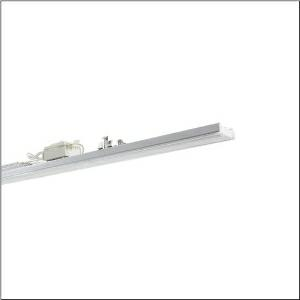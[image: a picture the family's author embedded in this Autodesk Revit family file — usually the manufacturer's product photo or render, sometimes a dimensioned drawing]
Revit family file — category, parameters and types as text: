
# Revit family: licross_21_recessed_ho_52tl12mn4fxm
name_source: partatom
category: Lighting Fixtures
units: mm (PartAtom-declared; Revit-internal decimal feet)

## family parameters
Cut with Voids When Loaded = No
Host = Face
Light Source = No
Part Type = Normal
Room Calculation Point = No
Round Connector Dimension = Use Diameter
Shared = No

## types (1)
- --- (1 x LED, 15100 lm, 83.1 W, 4000K)
    Apparent Load = 83 VA
    CIE Flux Codes = 69 91 98 100 100
    Color Rendering = 80
    Color Temperature = 4000K
    Default Elevation = 1800 mm
    Description = Licross 21 Recessed HO, luminaire insert, of sheet steel, galvanised, coil coated, white, length: 1.500mm, width: 66mm, height: 67mm, LED rated luminous flux: 15.100lm, light colour: 840, SDCM (Standard Deviation of Colour Matching)MacAdam ≤ 3 SDCM (initial), control gear: ON/OFF Multilumen, with plug, 3-pole, with phase selection, mains connection: 220..240V, AC, 50/60Hz, rated input power: 83W, internal wiring halogen-free, primary optical cover: cover, of PMMA, light emission: direct distribution, primary light characteristic: symmetric, protection rating (complete): IP40, insulation class (complete): insulation class I (protective earthing), certification: CE, ENEC, VDE, UKCA, protection symbol: D if used in an environment without relevant dust loads with corresponding accessories, impact resistance: IK06, permissible ambient temperature for indoor applications: -35..+30°C, corresponds to IFS (International Featured Standards) requirements for safety and quality in the food industry, reducing of maximum allowable ambient temperature of 5°C with ceiling mounting, LABS conformity tested according to VDMA 24364:2018-05, The light source and the operating device comply with the requirements of the Ecodesign Regulation (EU) 2019/2020 and are replaceable in accordance with this regulation, packaging unit: 1 piece
    Height = 58 mm
    Lamp = 1 x LED
    Lamp Light Flux = 15100 lm
    Lamp Power = 83.1 W
    Lamp count = 1
    Length = 1500 mm
    Luminous efficacy = 182 lm/W
    Manufacturer = Siteco
    ModVariant = No
    Model = 52TL12MN4FXM
    Mounting Place = Ceiling
    Mounting Type = Pendant
    Number of Poles = 1
    OnlyDefault = Yes
    Power Factor = 1
    Product Name = Licross 21 Recessed HO
    Product group = luminaire insert | ceiling pendant
    ProductGroupID = 901
    Protection Class = Protection class I
    Protection Degree = IP 40
    RLX_Detail_Level = 1
    RLX_Emergency_Light_Flux = 0 lm
    RLX_Emergency_Type = 0
    RLX_Emergency_Type_DB = No
    RlxData = <blob elided: 22589 chars, md5=74fb3a5b>
    Socket = socket
    Standby Power = 0 W
    System Light Flux = 15100 lm
    System Power = 83 W
    Type Comments = factory setting: luminous flux: 100 % | (A | C | E) | 195 mA
    Type Image = l_1296930.jpg
    URL = http://relux.com
    VarID = @adj_103073
    Voltage = 0 V
    Weight = 0.00 kg
    Width = 66 mm

## geometry (parser evidence)
native form markers: Blend x4, Sweep x11
no freeform markers — native parametric forms only
